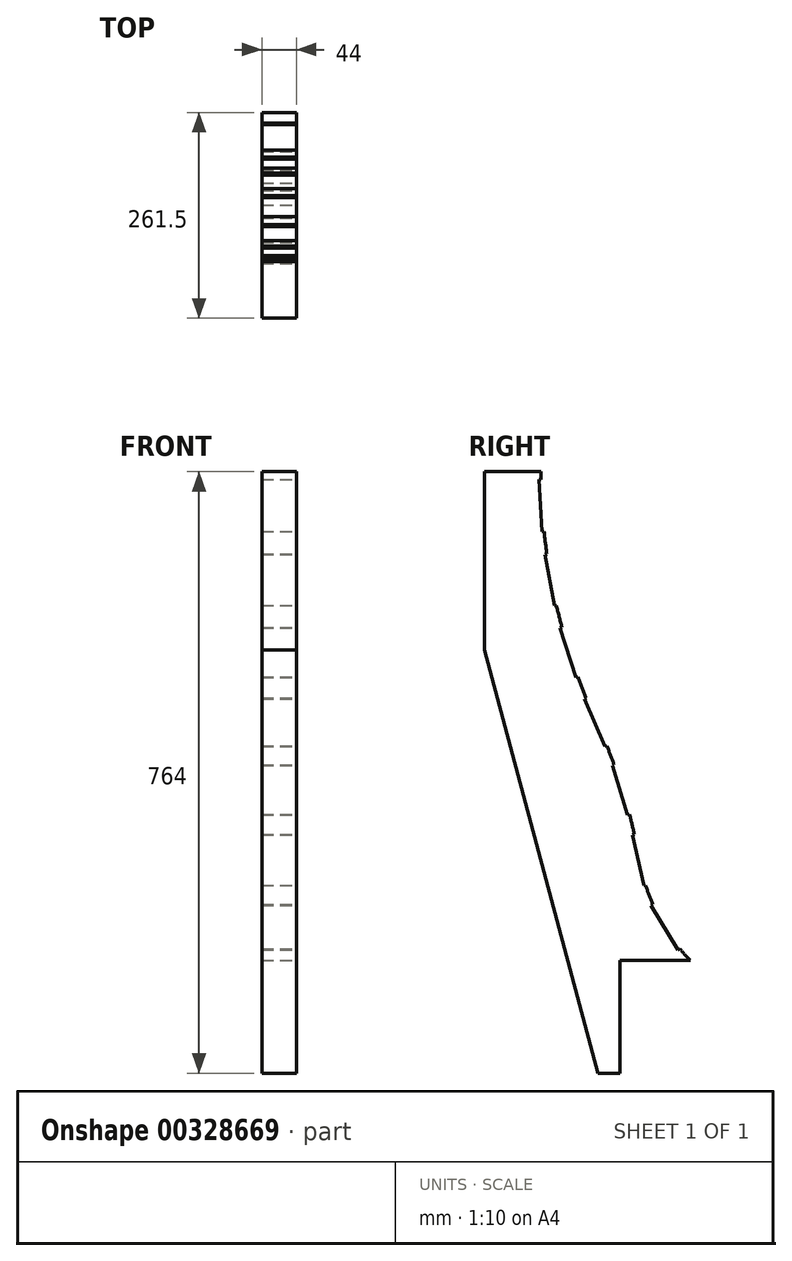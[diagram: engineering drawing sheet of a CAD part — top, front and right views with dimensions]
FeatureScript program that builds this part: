
annotation { "Feature Type Name" : "Feature", "Feature Type Description" : "" }
export const myFeature = defineFeature(function(context is Context, id is Id, definition is map)
    precondition{}
    {
        {
            var Q0;
            Q0=qCreatedBy(makeId("Right.planeOp"),FACE);
            var sketch = newSketch(context, id + "F0", { "sketchPlane" : qUnion([Q0])});
            skLineSegment(sketch, "E0", {"start": v(0, 0) * mm, "end": v(0, -143) * mm});
            skLineSegment(sketch, "E1", {"start": v(0, 0) * mm, "end": v(89.5, 0) * mm});
            skLineSegment(sketch, "E2", {"start": v(-28, -143) * mm, "end": v(-172, 394.42) * mm});
            skLineSegment(sketch, "E3", {"start": v(-172, 621) * mm, "end": v(-172, 394.42) * mm});
            skLineSegment(sketch, "E4", {"start": v(-172, 621) * mm, "end": v(-100, 621) * mm});
            skLineSegment(sketch, "E5", {"start": v(-100, 621) * mm, "end": v(650, 621) * mm, "construction": true});
            skArc(sketch, "E6", {"start": v(-100, 621) * mm, "mid": v(-82.65, 460.63) * mm, "end": v(-31.41, 307.67) * mm});
            skLineSegment(sketch, "E7", {"start": v(262, -57.45) * mm, "end": v(262, 167) * mm, "construction": true});
            skLineSegment(sketch, "E8", {"start": v(22, 167) * mm, "end": v(262, 167) * mm, "construction": true});
            skArc(sketch, "E9", {"start": v(25.68, 125.14) * mm, "mid": v(48.25, 57.87) * mm, "end": v(89.5, 0.14) * mm});
            skLineSegment(sketch, "E10", {"start": v(89.5, 0) * mm, "end": v(89.5, 0.14) * mm});
            skArc(sketch, "E11.filletArc", {"start": v(25.68, 125.14) * mm, "mid": v(2.97, 218.23) * mm, "end": v(-31.41, 307.67) * mm});
            skLineSegment(sketch, "E12", {"start": v(0, -143) * mm, "end": v(-28, -143) * mm});
            skSolve(sketch);
        }
        {
            var Q0;
            Q0=makeQuery(id+"F0.imprint","IMPRINT",FACE,{"disambiguationData":[TD([[makeQuery(id+"F0.imprint","IMPRINT",EDGE,{"derivedFrom":sQuery(id+"F0.wireOp",EDGE,"E0")}),-1.0]])]});
            extrude(context, id + "F1", {"entities" : qUnion([Q0]), "oppositeDirection" : true, "depth" : 44 * mm});
        }
        {
            var Q0;
            Q0=makeQuery(id+"F1.opExtrude","CAP_FACE",FACE,{"disambiguationData":[OSD([sQuery(id+"F0.wireOp",EDGE,"E0"),sQuery(id+"F0.wireOp",EDGE,"E1"),sQuery(id+"F0.wireOp",EDGE,"E2"),sQuery(id+"F0.wireOp",EDGE,"E3"),sQuery(id+"F0.wireOp",EDGE,"E4"),sQuery(id+"F0.wireOp",EDGE,"E6"),sQuery(id+"F0.wireOp",EDGE,"E9"),sQuery(id+"F0.wireOp",EDGE,"E10"),sQuery(id+"F0.wireOp",EDGE,"E11.filletArc"),sQuery(id+"F0.wireOp",EDGE,"E12")])],"isStart":true});
            var sketch = newSketch(context, id + "F2", { "sketchPlane" : qUnion([Q0])});
            skLineSegment(sketch, "E13", {"start": v(76.2, 15.08) * mm, "end": v(74.07, 13.78) * mm});
            skLineSegment(sketch, "E14", {"start": v(74.07, 13.78) * mm, "end": v(39.71, 70.13) * mm});
            skLineSegment(sketch, "E15", {"start": v(39.71, 70.13) * mm, "end": v(41.85, 71.43) * mm});
            skLineSegment(sketch, "E16", {"start": v(41.85, 71.43) * mm, "end": v(76.2, 15.08) * mm});
            skLineSegment(sketch, "E17", {"start": v(32.8, 95.8) * mm, "end": v(30.36, 95.27) * mm});
            skLineSegment(sketch, "E18", {"start": v(30.36, 95.27) * mm, "end": v(16.15, 159.72) * mm});
            skLineSegment(sketch, "E19", {"start": v(16.15, 159.72) * mm, "end": v(18.6, 160.26) * mm});
            skLineSegment(sketch, "E20", {"start": v(18.6, 160.26) * mm, "end": v(19.72, 160.5) * mm});
            skLineSegment(sketch, "E21", {"start": v(19.72, 160.5) * mm, "end": v(32.8, 95.8) * mm});
            skLineSegment(sketch, "E22", {"start": v(12.4, 185.5) * mm, "end": v(10.01, 184.77) * mm});
            skLineSegment(sketch, "E23", {"start": v(10.01, 184.77) * mm, "end": v(-9.6, 247.78) * mm});
            skLineSegment(sketch, "E24", {"start": v(-9.6, 247.78) * mm, "end": v(-7.21, 248.53) * mm});
            skLineSegment(sketch, "E25", {"start": v(-7.21, 248.53) * mm, "end": v(-3.2, 249.83) * mm});
            skLineSegment(sketch, "E26", {"start": v(-3.2, 249.83) * mm, "end": v(12.4, 185.5) * mm});
            skLineSegment(sketch, "E27", {"start": v(-16.45, 272.83) * mm, "end": v(-18.74, 271.84) * mm});
            skLineSegment(sketch, "E28", {"start": v(-18.74, 271.84) * mm, "end": v(-44.96, 332.4) * mm});
            skLineSegment(sketch, "E29", {"start": v(-44.96, 332.4) * mm, "end": v(-42.67, 333.4) * mm});
            skLineSegment(sketch, "E30", {"start": v(-42.67, 333.4) * mm, "end": v(-40.19, 334.48) * mm});
            skLineSegment(sketch, "E31", {"start": v(-40.19, 334.48) * mm, "end": v(-16.45, 272.83) * mm});
            skLineSegment(sketch, "E32", {"start": v(-53.27, 360.4) * mm, "end": v(-55.65, 359.63) * mm});
            skLineSegment(sketch, "E33", {"start": v(-55.65, 359.63) * mm, "end": v(-75.84, 422.47) * mm});
            skLineSegment(sketch, "E34", {"start": v(-75.84, 422.47) * mm, "end": v(-73.46, 423.23) * mm});
            skLineSegment(sketch, "E35", {"start": v(-73.46, 423.23) * mm, "end": v(-53.27, 360.4) * mm});
            skLineSegment(sketch, "E36", {"start": v(-95.1, 515.77) * mm, "end": v(-92.65, 516.23) * mm});
            skLineSegment(sketch, "E37", {"start": v(-95.1, 515.77) * mm, "end": v(-83.02, 450.89) * mm});
            skLineSegment(sketch, "E38", {"start": v(-83.02, 450.89) * mm, "end": v(-80.56, 451.35) * mm});
            skLineSegment(sketch, "E39", {"start": v(-92.65, 516.23) * mm, "end": v(-80.56, 451.35) * mm});
            skLineSegment(sketch, "E40", {"start": v(-96.16, 545.23) * mm, "end": v(-98.66, 545.23) * mm});
            skLineSegment(sketch, "E41", {"start": v(-98.66, 545.23) * mm, "end": v(-102.44, 611.23) * mm});
            skLineSegment(sketch, "E42", {"start": v(-102.44, 611.23) * mm, "end": v(-99.94, 611.23) * mm});
            skLineSegment(sketch, "E43", {"start": v(-99.94, 611.23) * mm, "end": v(-96.16, 545.23) * mm});
            skSolve(sketch);
        }
        {
            var Q0;
            Q0=qSketchRegion(id+"F2",true);
            extrude(context, id + "F3", {"entities" : qUnion([Q0]), "operationType" : NewBodyOperationType.REMOVE, "endBound" : BoundingType.THROUGH_ALL, "oppositeDirection" : true, "depth" : 25 * mm});
        }
    });
